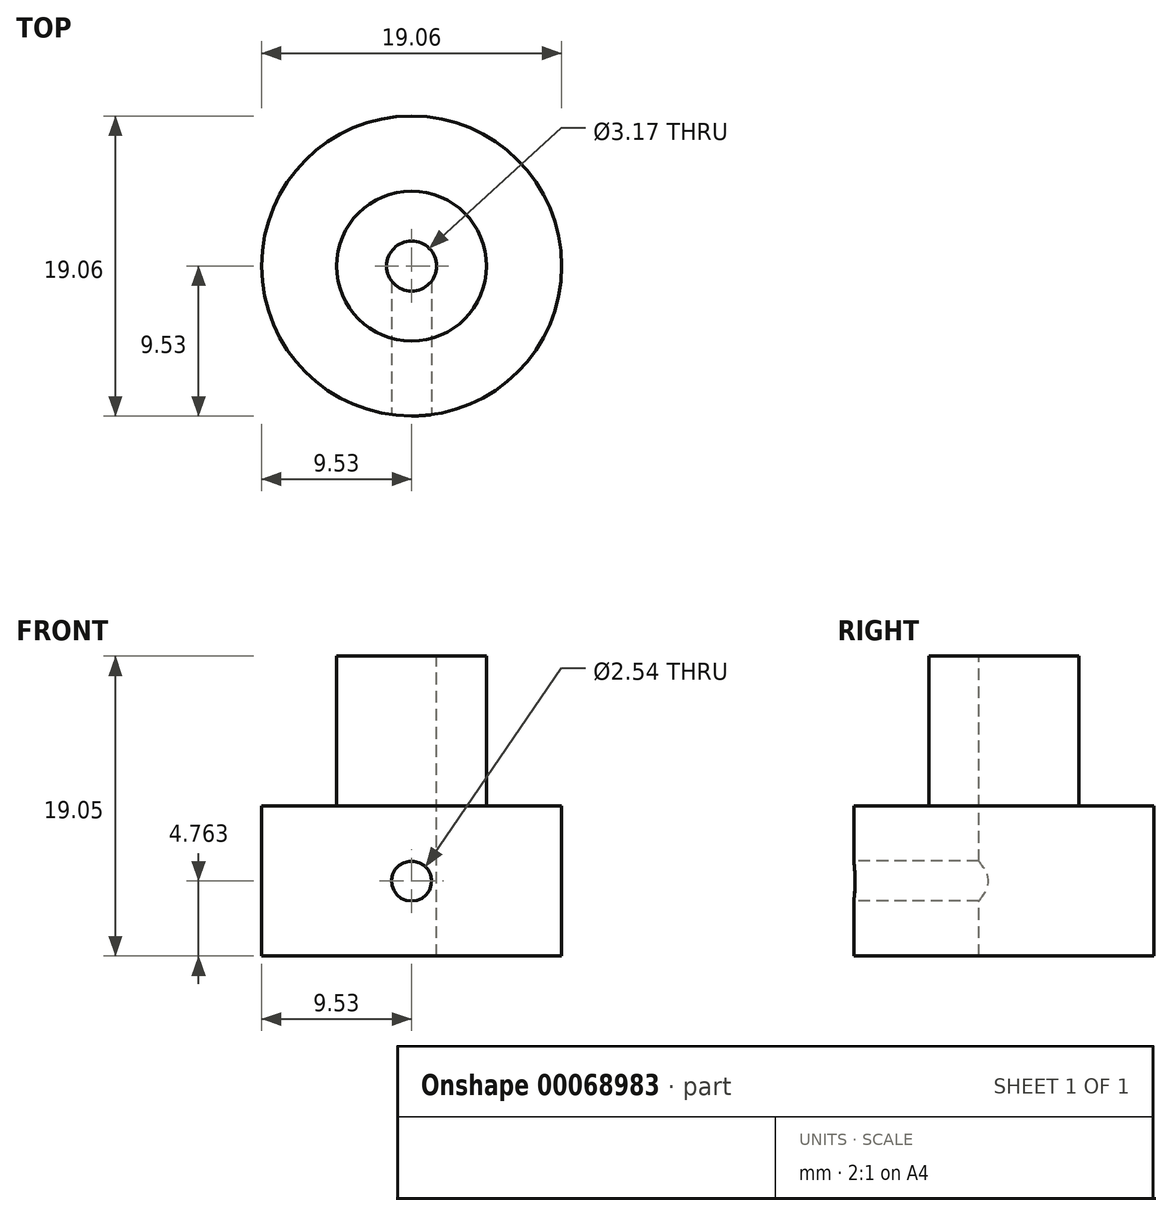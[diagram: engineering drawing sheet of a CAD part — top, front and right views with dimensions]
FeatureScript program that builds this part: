
annotation { "Feature Type Name" : "Feature", "Feature Type Description" : "" }
export const myFeature = defineFeature(function(context is Context, id is Id, definition is map)
    precondition{}
    {
        {
            var Q0;
            Q0=qCreatedBy(makeId("Top.planeOp"),FACE);
            var sketch = newSketch(context, id + "F0", { "sketchPlane" : qUnion([Q0])});
            skCircle(sketch, "E0", {"center": v(0, 0) * mm, "radius": 9.53 * mm});
            skSolve(sketch);
        }
        {
            var Q0;
            Q0 = qSketchRegion(id + "F0", true);
            extrude(context, id + "F1", {"entities" : qUnion([Q0]), "depth" : 9.52 * mm});
        }
        {
            var Q0;
            Q0=makeQuery(id+"F1.opExtrude","CAP_FACE",FACE,{"disambiguationData":[OSD([sQuery(id+"F0.wireOp",EDGE,"E0")])],"isStart":false});
            var sketch = newSketch(context, id + "F2", { "sketchPlane" : qUnion([Q0])});
            skCircle(sketch, "E1", {"center": v(0, 0) * mm, "radius": 4.76 * mm});
            skSolve(sketch);
        }
        {
            var Q0;
            Q0 = qSketchRegion(id + "F2", true);
            extrude(context, id + "F3", {"entities" : qUnion([Q0]), "operationType" : NewBodyOperationType.ADD, "depth" : 9.52 * mm});
        }
        {
            var Q0;
            Q0=makeQuery(id+"F3.opExtrude","CAP_FACE",FACE,{"disambiguationData":[OSD([sQuery(id+"F2.wireOp",EDGE,"E1")])],"isStart":false});
            var sketch = newSketch(context, id + "F4", { "sketchPlane" : qUnion([Q0])});
            skCircle(sketch, "E2", {"center": v(0, 0) * mm, "radius": 1.59 * mm});
            skSolve(sketch);
        }
        {
            var Q0;
            Q0=qCreatedBy(makeId("Front.planeOp"),FACE);
            cPlane(context, id + "F5", {"entities" : qUnion([Q0]), "cplaneType" : CPlaneType.OFFSET, "offset" : 9.52 * mm, "width" : 152.4 * mm, "height" : 152.4 * mm});
        }
        {
            var Q0;
            Q0=qCreatedBy(id+"F5.planeOp",FACE);
            var sketch = newSketch(context, id + "F6", { "sketchPlane" : qUnion([Q0])});
            skLineSegment(sketch, "E3.0", {"start": v(-9.53, 9.53) * mm, "end": v(9.53, 9.53) * mm});
            skPoint(sketch, "E4.0", {"position": v(0, 0) * mm});
            skLineSegment(sketch, "E5.0", {"start": v(-9.53, 0) * mm, "end": v(9.53, 0) * mm});
            skLineSegment(sketch, "E6", {"start": v(0, 0) * mm, "end": v(0, 9.53) * mm, "construction": true});
            skCircle(sketch, "E7", {"center": v(0, 4.76) * mm, "radius": 1.27 * mm});
            skSolve(sketch);
        }
        {
            var Q0;
            Q0 = qSketchRegion(id + "F6", true);
            extrude(context, id + "F7", {"entities" : qUnion([Q0]), "operationType" : NewBodyOperationType.REMOVE, "oppositeDirection" : true, "depth" : 9.52 * mm});
        }
        {
            var Q0;
            Q0 = qSketchRegion(id + "F4", true);
            extrude(context, id + "F8", {"entities" : qUnion([Q0]), "operationType" : NewBodyOperationType.REMOVE, "endBound" : BoundingType.THROUGH_ALL, "oppositeDirection" : true, "depth" : 25.4 * mm});
        }
    });
